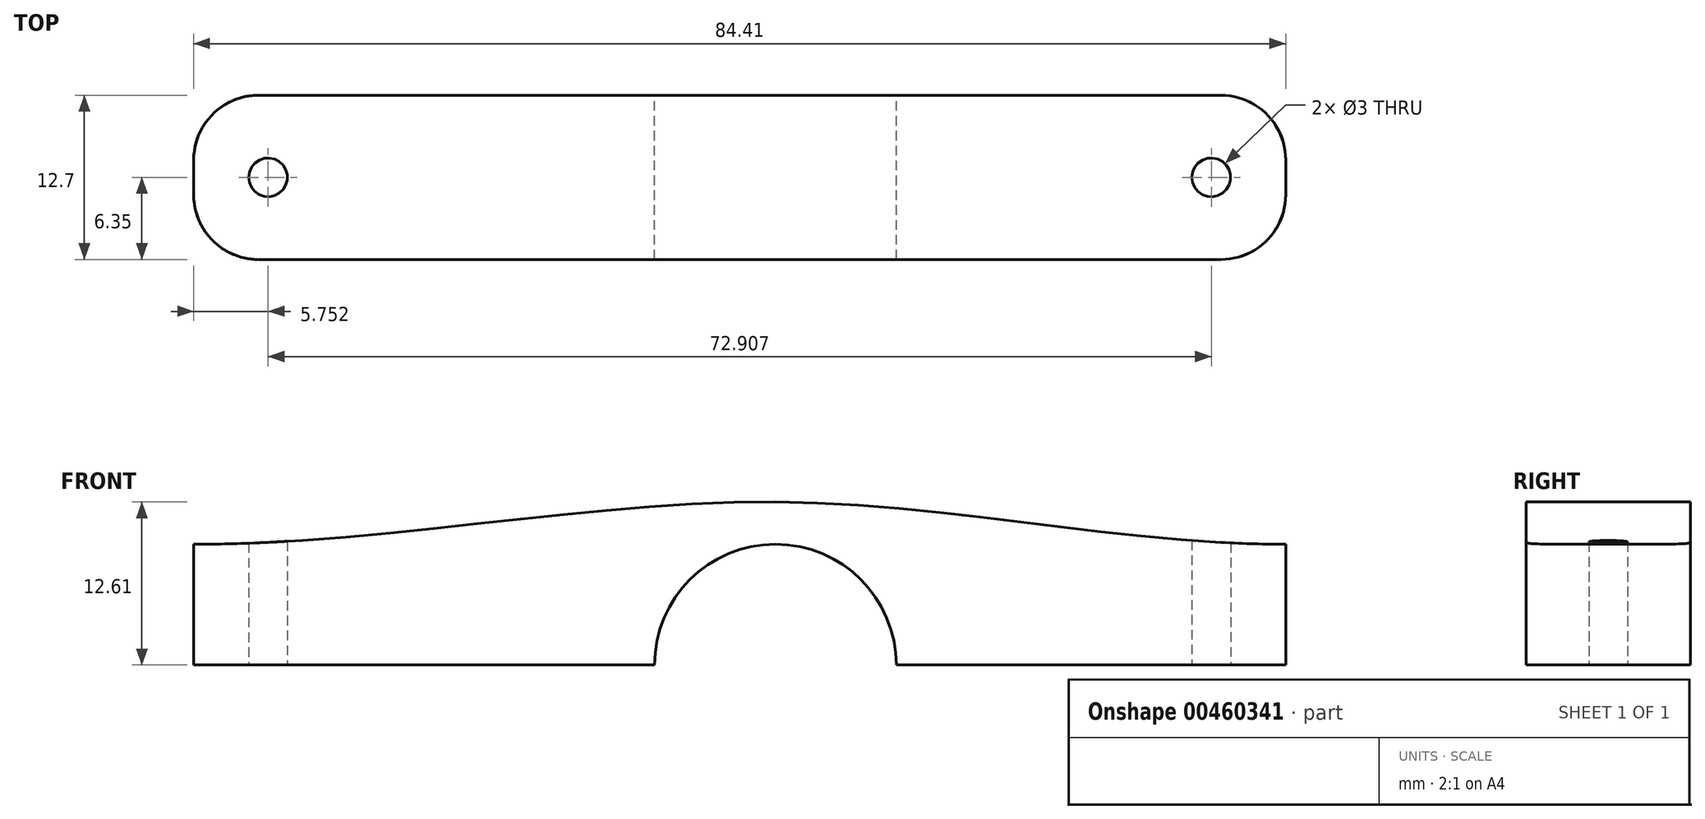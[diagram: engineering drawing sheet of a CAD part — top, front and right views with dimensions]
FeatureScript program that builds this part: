
annotation { "Feature Type Name" : "Feature", "Feature Type Description" : "" }
export const myFeature = defineFeature(function(context is Context, id is Id, definition is map)
    precondition{}
    {
        {
            var Q0;
            Q0=qCreatedBy(makeId("Front.planeOp"),FACE);
            var sketch = newSketch(context, id + "F0", { "sketchPlane" : qUnion([Q0])});
            skLineSegment(sketch, "E0.bottom", {"start": v(39.44, 0) * mm, "end": v(9.34, 0) * mm});
            skLineSegment(sketch, "E0.left", {"start": v(39.44, 0) * mm, "end": v(39.44, 9.34) * mm});
            skLineSegment(sketch, "E0.right", {"start": v(-44.97, 0) * mm, "end": v(-44.97, 9.34) * mm});
            skPoint(sketch, "E0.middle", {"position": v(-2.76, 4.67) * mm});
            skLineSegment(sketch, "E1.trimOffspring", {"start": v(0, 9.34) * mm, "end": v(-44.97, 9.34) * mm});
            skLineSegment(sketch, "E2.trimOffspring", {"start": v(-9.34, 0) * mm, "end": v(-44.97, 0) * mm});
            skArc(sketch, "E3", {"start": v(9.34, 0) * mm, "mid": v(0, 9.34) * mm, "end": v(-9.34, 0) * mm});
            skLineSegment(sketch, "E4", {"start": v(39.44, 9.34) * mm, "end": v(0, 9.34) * mm});
            skFitSpline(sketch, "E5", {"points": [v(-44.97, 9.34) * mm, v(0, 12.61) * mm, v(39.44, 9.34) * mm], "startDerivative": vector(88.77, 0) * mm, "endDerivative": vector(81.14, 0) * mm});
            skSolve(sketch);
        }
        {
            var Q0;
            Q0=qSketchRegion(id+"F0",true);
            extrude(context, id + "F1", {"entities" : qUnion([Q0]), "depth" : 12.7 * mm});
        }
        {
            var Q0;
            Q0=makeQuery(id+"F1.opExtrude","CAP_EDGE",EDGE,{"disambiguationData":[OSD([sQuery(id+"F0.wireOp",EDGE,"E0.right")])],"isStart":false});
            var Q1;
            Q1=makeQuery(id+"F1.opExtrude","CAP_EDGE",EDGE,{"disambiguationData":[OSD([sQuery(id+"F0.wireOp",EDGE,"E0.right")])],"isStart":true});
            var Q2;
            Q2=makeQuery(id+"F1.opExtrude","CAP_EDGE",EDGE,{"disambiguationData":[OSD([sQuery(id+"F0.wireOp",EDGE,"E0.left")])],"isStart":false});
            var Q3;
            Q3=makeQuery(id+"F1.opExtrude","CAP_EDGE",EDGE,{"disambiguationData":[OSD([sQuery(id+"F0.wireOp",EDGE,"E0.left")])],"isStart":true});
            fillet(context, id + "F2", {"entities" : qUnion([Q0, Q1, Q2, Q3]), "radius" : 5 * mm, "tangentPropagation" : true, "allowEdgeOverflow" : false});
        }
        {
            var Q0;
            Q0=qCreatedBy(makeId("Top.planeOp"),FACE);
            var sketch = newSketch(context, id + "F3", { "sketchPlane" : qUnion([Q0])});
            skLineSegment(sketch, "E6", {"start": v(-45.81, -6.35) * mm, "end": v(40.65, -6.35) * mm, "construction": true});
            skCircle(sketch, "E7", {"center": v(-39.22, -6.35) * mm, "radius": 1.5 * mm});
            skCircle(sketch, "E8", {"center": v(33.69, -6.35) * mm, "radius": 1.5 * mm});
            skSolve(sketch);
        }
        {
            var Q0;
            Q0=qSketchRegion(id+"F3",true);
            extrude(context, id + "F4", {"entities" : qUnion([Q0]), "operationType" : NewBodyOperationType.REMOVE, "depth" : 19.1 * mm});
        }
    });
